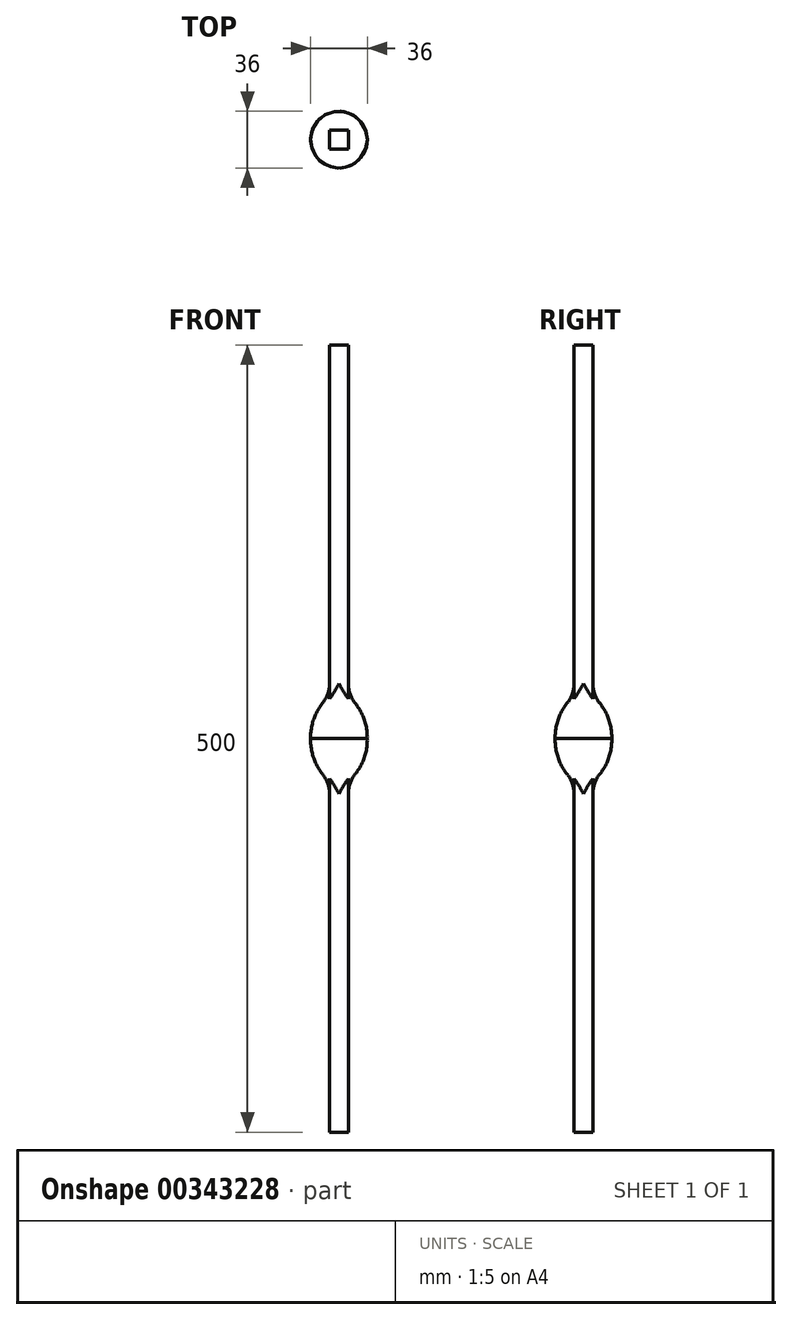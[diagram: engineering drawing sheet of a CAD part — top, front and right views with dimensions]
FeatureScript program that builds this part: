
annotation { "Feature Type Name" : "Feature", "Feature Type Description" : "" }
export const myFeature = defineFeature(function(context is Context, id is Id, definition is map)
    precondition{}
    {
        {
            var Q0;
            Q0=qCreatedBy(makeId("Front.planeOp"),FACE);
            var sketch = newSketch(context, id + "F0", { "sketchPlane" : qUnion([Q0])});
            skLineSegment(sketch, "E0", {"start": v(0, 40) * mm, "end": v(6, 40) * mm});
            skLineSegment(sketch, "E1", {"start": v(6, 40) * mm, "end": v(6, 35) * mm});
            skArc(sketch, "E2", {"start": v(6, 35) * mm, "mid": v(7.12, 28.4) * mm, "end": v(10.36, 22.53) * mm});
            skArc(sketch, "E3", {"start": v(10.36, 22.53) * mm, "mid": v(16.15, 11.93) * mm, "end": v(17.99, 0) * mm});
            skLineSegment(sketch, "E4.MirrorCS", {"start": v(0, -40) * mm, "end": v(6, -40) * mm});
            skLineSegment(sketch, "E5.MirrorCS", {"start": v(6, -40) * mm, "end": v(6, -35) * mm});
            skArc(sketch, "E6.MirrorCS", {"start": v(6, -35) * mm, "mid": v(7.12, -28.4) * mm, "end": v(10.36, -22.53) * mm});
            skArc(sketch, "E7.MirrorCS", {"start": v(10.36, -22.53) * mm, "mid": v(16.15, -11.93) * mm, "end": v(17.99, 0) * mm});
            skLineSegment(sketch, "E8", {"start": v(0, 40) * mm, "end": v(0, -40) * mm});
            skSolve(sketch);
        }
        {
            var Q0;
            Q0=makeQuery(id+"F0.imprint","IMPRINT",FACE,{"disambiguationData":[TD([[makeQuery(id+"F0.imprint","IMPRINT",EDGE,{"derivedFrom":sQuery(id+"F0.wireOp",EDGE,"E0")}),-1.0]])]});
            var Q1;
            Q1=sQuery(id+"F0.wireOp",EDGE,"E8");
            revolve(context, id + "F1", {"entities" : qUnion([Q0]), "axis" : qUnion([Q1]), "revolveType" : RevolveType.FULL});
        }
        {
            var Q0;
            Q0=makeQuery(id+"F1.opRevolve","SWEPT_FACE",FACE,{"disambiguationData":[OSD([sQuery(id+"F0.wireOp",EDGE,"E0")])]});
            var sketch = newSketch(context, id + "F2", { "sketchPlane" : qUnion([Q0])});
            skLineSegment(sketch, "E9.bottom", {"start": v(6, 6) * mm, "end": v(-6, 6) * mm});
            skLineSegment(sketch, "E9.top", {"start": v(6, -6) * mm, "end": v(-6, -6) * mm});
            skLineSegment(sketch, "E9.left", {"start": v(6, 6) * mm, "end": v(6, -6) * mm});
            skLineSegment(sketch, "E9.right", {"start": v(-6, 6) * mm, "end": v(-6, -6) * mm});
            skPoint(sketch, "E9.middle", {"position": v(0, 0) * mm});
            skSolve(sketch);
        }
        {
            var Q0;
            {var subQ0=sQuery(id+"F2.wireOp",EDGE,"E9.left");var subQ1=sQuery(id+"F2.wireOp",EDGE,"E9.bottom");var subQ2=makeQuery(id+"F2.imprint","INTERSECT",VERTEX,{"derivedFrom":[subQ1,subQ0]});Q0=makeQuery(id+"F2.imprint","IMPRINT",FACE,{"disambiguationData":[TD([[makeQuery(id+"F2.imprint","IMPRINT",EDGE,{"disambiguationData":[TD([[subQ2,-1.0]])],"derivedFrom":subQ1}),1.0]])]});}
            var Q1;
            {var subQ0=sQuery(id+"F2.wireOp",EDGE,"E9.right");var subQ1=sQuery(id+"F2.wireOp",EDGE,"E9.bottom");var subQ2=makeQuery(id+"F2.imprint","INTERSECT",VERTEX,{"derivedFrom":[subQ1,subQ0]});Q1=makeQuery(id+"F2.imprint","IMPRINT",FACE,{"disambiguationData":[TD([[makeQuery(id+"F2.imprint","IMPRINT",EDGE,{"disambiguationData":[TD([[subQ2,1.0]])],"derivedFrom":subQ1}),1.0]])]});}
            var Q2;
            {var subQ0=sQuery(id+"F2.wireOp",EDGE,"E9.right");var subQ1=sQuery(id+"F2.wireOp",EDGE,"E9.top");var subQ2=makeQuery(id+"F2.imprint","INTERSECT",VERTEX,{"derivedFrom":[subQ1,subQ0]});Q2=makeQuery(id+"F2.imprint","IMPRINT",FACE,{"disambiguationData":[TD([[makeQuery(id+"F2.imprint","IMPRINT",EDGE,{"disambiguationData":[TD([[subQ2,1.0]])],"derivedFrom":subQ1}),-1.0]])]});}
            var Q3;
            {var subQ0=sQuery(id+"F2.wireOp",EDGE,"E9.left");var subQ1=sQuery(id+"F2.wireOp",EDGE,"E9.top");var subQ2=makeQuery(id+"F2.imprint","INTERSECT",VERTEX,{"derivedFrom":[subQ1,subQ0]});Q3=makeQuery(id+"F2.imprint","IMPRINT",FACE,{"disambiguationData":[TD([[makeQuery(id+"F2.imprint","IMPRINT",EDGE,{"disambiguationData":[TD([[subQ2,-1.0]])],"derivedFrom":subQ1}),-1.0]])]});}
            var Q4;
            {var subQ0=makeQuery(id+"F1.opRevolve","SWEPT_EDGE",EDGE,{"disambiguationData":[OSD([sQuery(id+"F0.wireOp",EDGE,"E0"),sQuery(id+"F0.wireOp",EDGE,"E1")])]});var subQ1=makeQuery(id+"F2.imprint","INTERSECT",VERTEX,{"derivedFrom":[subQ0,sQuery(id+"F2.wireOp",EDGE,"E9.bottom")]});Q4=makeQuery(id+"F2.imprint","IMPRINT",FACE,{"disambiguationData":[TD([[makeQuery(id+"F2.imprint","IMPRINT",EDGE,{"disambiguationData":[TD([[subQ1,1.0]])],"derivedFrom":subQ0}),1.0]])]});}
            extrude(context, id + "F3", {"entities" : qUnion([Q0, Q1, Q2, Q3, Q4]), "operationType" : NewBodyOperationType.ADD, "depth" : 210 * mm, "hasSecondDirection" : true, "secondDirectionOppositeDirection" : true, "secondDirectionDepth" : 25 * mm});
        }
        {
            var Q0;
            Q0=makeQuery(id+"F1.opRevolve","SWEPT_FACE",FACE,{"disambiguationData":[OSD([sQuery(id+"F0.wireOp",EDGE,"E4.MirrorCS")])]});
            var sketch = newSketch(context, id + "F4", { "sketchPlane" : qUnion([Q0])});
            skLineSegment(sketch, "E10.bottom", {"start": v(6, 6) * mm, "end": v(-6, 6) * mm});
            skLineSegment(sketch, "E10.top", {"start": v(6, -6) * mm, "end": v(-6, -6) * mm});
            skLineSegment(sketch, "E10.left", {"start": v(6, 6) * mm, "end": v(6, -6) * mm});
            skLineSegment(sketch, "E10.right", {"start": v(-6, 6) * mm, "end": v(-6, -6) * mm});
            skPoint(sketch, "E10.middle", {"position": v(0, 0) * mm});
            skSolve(sketch);
        }
        {
            var Q0;
            {var subQ0=sQuery(id+"F4.wireOp",EDGE,"E10.right");var subQ1=sQuery(id+"F4.wireOp",EDGE,"E10.bottom");var subQ2=makeQuery(id+"F4.imprint","INTERSECT",VERTEX,{"derivedFrom":[subQ1,subQ0]});Q0=makeQuery(id+"F4.imprint","IMPRINT",FACE,{"disambiguationData":[TD([[makeQuery(id+"F4.imprint","IMPRINT",EDGE,{"disambiguationData":[TD([[subQ2,1.0]])],"derivedFrom":subQ1}),1.0]])]});}
            var Q1;
            {var subQ0=sQuery(id+"F4.wireOp",EDGE,"E10.left");var subQ1=sQuery(id+"F4.wireOp",EDGE,"E10.bottom");var subQ2=makeQuery(id+"F4.imprint","INTERSECT",VERTEX,{"derivedFrom":[subQ1,subQ0]});Q1=makeQuery(id+"F4.imprint","IMPRINT",FACE,{"disambiguationData":[TD([[makeQuery(id+"F4.imprint","IMPRINT",EDGE,{"disambiguationData":[TD([[subQ2,-1.0]])],"derivedFrom":subQ1}),1.0]])]});}
            var Q2;
            {var subQ0=sQuery(id+"F4.wireOp",EDGE,"E10.left");var subQ1=sQuery(id+"F4.wireOp",EDGE,"E10.top");var subQ2=makeQuery(id+"F4.imprint","INTERSECT",VERTEX,{"derivedFrom":[subQ1,subQ0]});Q2=makeQuery(id+"F4.imprint","IMPRINT",FACE,{"disambiguationData":[TD([[makeQuery(id+"F4.imprint","IMPRINT",EDGE,{"disambiguationData":[TD([[subQ2,-1.0]])],"derivedFrom":subQ1}),-1.0]])]});}
            var Q3;
            {var subQ0=sQuery(id+"F4.wireOp",EDGE,"E10.right");var subQ1=sQuery(id+"F4.wireOp",EDGE,"E10.top");var subQ2=makeQuery(id+"F4.imprint","INTERSECT",VERTEX,{"derivedFrom":[subQ1,subQ0]});Q3=makeQuery(id+"F4.imprint","IMPRINT",FACE,{"disambiguationData":[TD([[makeQuery(id+"F4.imprint","IMPRINT",EDGE,{"disambiguationData":[TD([[subQ2,1.0]])],"derivedFrom":subQ1}),-1.0]])]});}
            var Q4;
            {var subQ0=makeQuery(id+"F1.opRevolve","SWEPT_EDGE",EDGE,{"disambiguationData":[OSD([sQuery(id+"F0.wireOp",EDGE,"E4.MirrorCS"),sQuery(id+"F0.wireOp",EDGE,"E5.MirrorCS")])]});var subQ1=makeQuery(id+"F4.imprint","INTERSECT",VERTEX,{"derivedFrom":[subQ0,sQuery(id+"F4.wireOp",EDGE,"E10.bottom")]});Q4=makeQuery(id+"F4.imprint","IMPRINT",FACE,{"disambiguationData":[TD([[makeQuery(id+"F4.imprint","IMPRINT",EDGE,{"disambiguationData":[TD([[subQ1,-1.0]])],"derivedFrom":subQ0}),-1.0]])]});}
            extrude(context, id + "F5", {"entities" : qUnion([Q0, Q1, Q2, Q3, Q4]), "operationType" : NewBodyOperationType.ADD, "depth" : 210 * mm, "hasSecondDirection" : true, "secondDirectionOppositeDirection" : true, "secondDirectionDepth" : 25 * mm});
        }
    });
